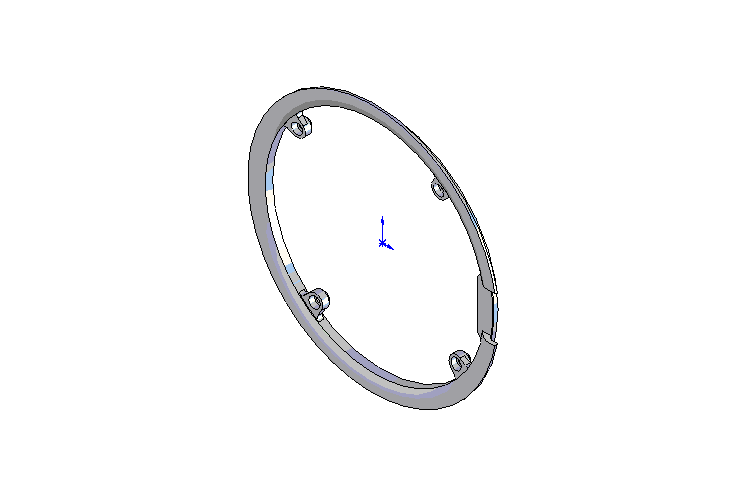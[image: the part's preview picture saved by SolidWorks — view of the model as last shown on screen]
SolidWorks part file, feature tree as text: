
SOLIDWORKS PART (.sldprt)
format: sldprt  version: not decoded by parser v0  size: 709,632 bytes
history: native  units: mm
features: sketch x8, plane x4, cut_extrude x3, extrude x3, material x1, revolve x1, chamfer x1, cut_revolve x1 (+10 scaffold rows collapsed)
feature tree (32):
  scaffold x10  (default folders/planes/origin — collapsed)
  material  "Matériau <non spécifié>"
  plane  "Plan de face"
  plane  "Plan de dessus"
  plane  "Plan de droite"
  plane  "Plan1"
  sketch  "Esquisse1"  dims[D3=3.0mm D1=2.0mm D2=6.5mm D4=210.0mm D5=195.0mm D6=9.0mm D7=175.0mm D8=7.0mm D9=~17.515697mm]
  revolve  "Révolution1"  Angle=360deg
  sketch  "Esquisse2"  dims[c1.D1=170.0mm c1.D3=5.5mm c1.D4=13.0mm c1.D5=185.0mm c1.D6=3.0mm c1.D12=3.0mm c2.D3=185.0mm c2.D2=~134.021591mm c3.D2=38.0deg c3.D7=~13.703857mm c4.D7=20.0deg c4.D8=~105.610455mm c5.D8=90.0deg c5.D9=42.0mm c5.D10=~23.545531mm c6.D10=90.0deg c6.D11=177.0mm c6.D4=177.0mm]
  cut_extrude  "Enlèv. mat.-Extru.2"  [1 undecoded]
  sketch  "Esquisse3"  dims[D1=35.0mm]
  cut_extrude  "Enlèv. mat.-Extru.3"  [1 undecoded]
  sketch  "Esquisse4"  dims[c1.D1=92.5mm c1.D2=2.0mm c2.D1=177.0mm]
  extrude  "Extrusion1"  [1 undecoded]
  sketch  "Esquisse5"  dims[c1.D2=170.0mm c1.D3=13.0mm c1.D4=5.5mm c2.D3=3.0mm c2.D6=6.5mm c2.D1=105.0mm c3.D1=38.0deg c3.D5=~10.914586mm c4.D5=20.0deg c4.D1=~94.816367mm c5.D1=90.0deg]
  extrude  "Extrusion2"  Depth=4.5mm
  sketch  "Esquisse6"
  extrude  "Extrusion4"  Depth=4mm
  chamfer  "Chanfrein1"  Distance=3mm Angle=45deg
  sketch  "Esquisse7"  dims[c1.D1=~14.520316mm c2.D1=5.0deg]
  cut_revolve  "Enlèvement de matière-Révolution1"  Angle=286deg
  sketch  "Esquisse8"  dims[D1=9.0mm]
  cut_extrude  "Enlèv. mat.-Extru.4"  [1 undecoded]
decode coverage: 12 of 17 modeling features carry decoded parameters
note: ~ marks probable driven/reference dimensions
note: 4 parameter values undecoded
summary: no parameter record found for 4 features
note: suppression state not decoded; provenance and decode notes live in map.json
